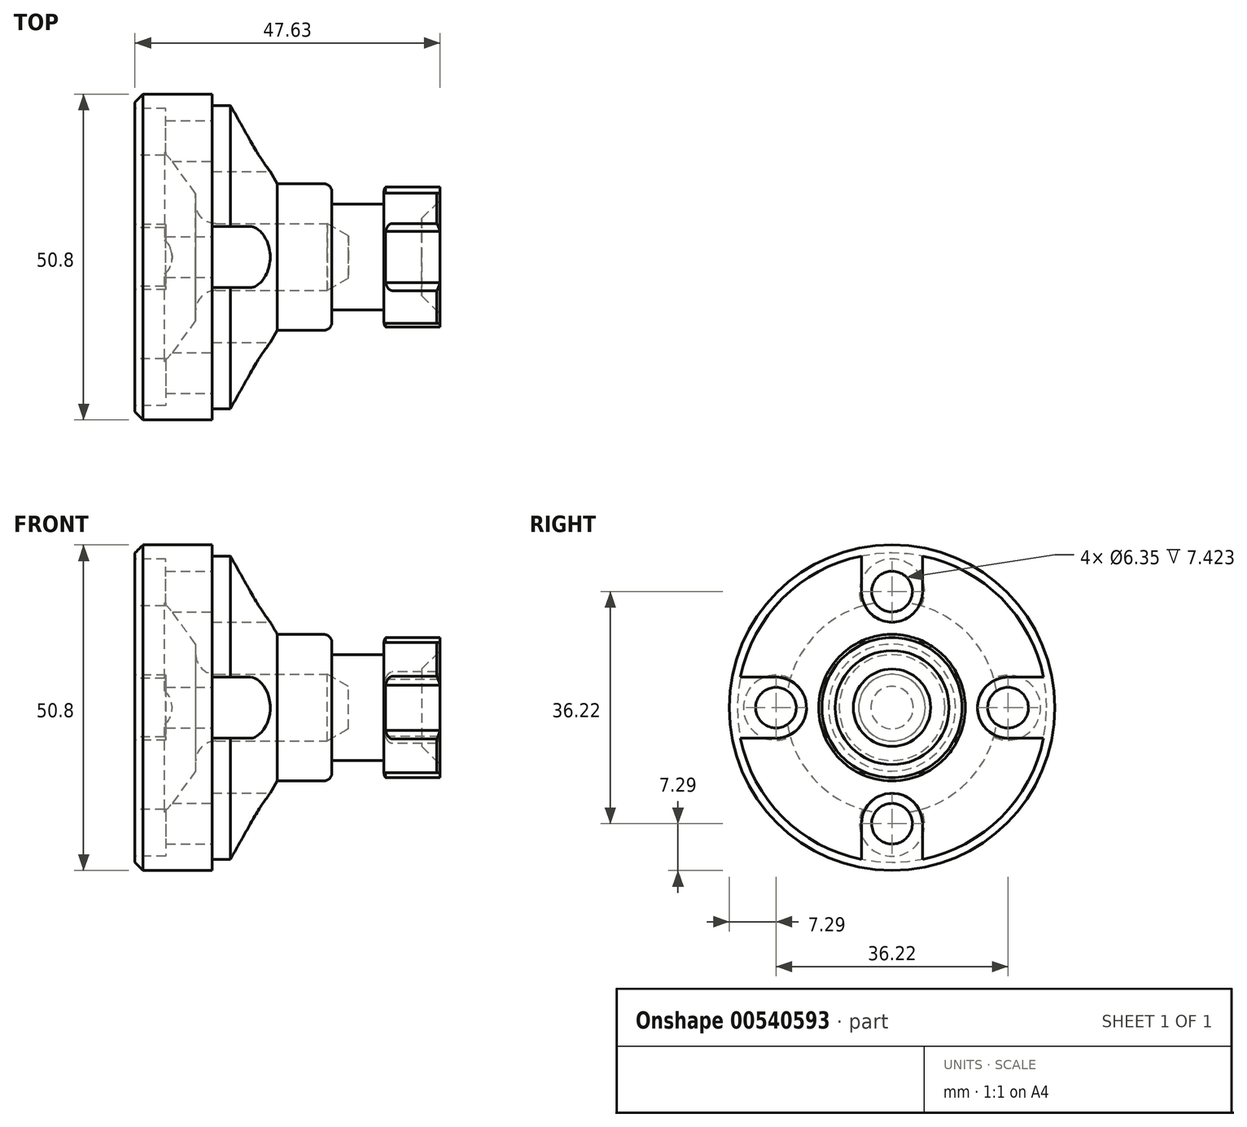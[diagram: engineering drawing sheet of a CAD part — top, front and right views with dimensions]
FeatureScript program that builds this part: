
annotation { "Feature Type Name" : "Feature", "Feature Type Description" : "" }
export const myFeature = defineFeature(function(context is Context, id is Id, definition is map)
    precondition{}
    {
        {
            var Q0;
            Q0=qCreatedBy(makeId("Front.planeOp"),FACE);
            var sketch = newSketch(context, id + "F0", { "sketchPlane" : qUnion([Q0])});
            skLineSegment(sketch, "E0", {"start": v(0, 0) * mm, "end": v(0, 10.92) * mm});
            skLineSegment(sketch, "E1", {"start": v(-35.56, 25.4) * mm, "end": v(-46.36, 25.4) * mm});
            skLineSegment(sketch, "E2", {"start": v(-47.63, 24.13) * mm, "end": v(-47.63, 0) * mm});
            skLineSegment(sketch, "E3", {"start": v(-47.63, 0) * mm, "end": v(0, 0) * mm});
            skLineSegment(sketch, "E4", {"start": v(-0.5, 11.43) * mm, "end": v(-7.5, 11.43) * mm});
            skLineSegment(sketch, "E5", {"start": v(-8.76, 10.16) * mm, "end": v(-8.76, 8.25) * mm});
            skLineSegment(sketch, "E6", {"start": v(-8.76, 8.25) * mm, "end": v(-16.9, 8.25) * mm});
            skLineSegment(sketch, "E7", {"start": v(-16.9, 10.16) * mm, "end": v(-16.9, 8.25) * mm});
            skLineSegment(sketch, "E8", {"start": v(-18.16, 11.43) * mm, "end": v(-25.4, 11.43) * mm});
            skLineSegment(sketch, "E9", {"start": v(-25.4, 11.43) * mm, "end": v(-32.73, 24.13) * mm});
            skLineSegment(sketch, "E10", {"start": v(-47.63, 0) * mm, "end": v(-47.63, 24.13) * mm, "construction": true});
            skLineSegment(sketch, "E11", {"start": v(-47.63, 24.13) * mm, "end": v(-46.36, 25.4) * mm});
            skPoint(sketch, "E12.orphan", {"position": v(-47.63, 25.4) * mm});
            skPoint(sketch, "E13.visualSharp", {"position": v(-16.9, 11.43) * mm});
            skArc(sketch, "E13.filletArc", {"start": v(-16.9, 10.16) * mm, "mid": v(-17.26, 11.06) * mm, "end": v(-18.16, 11.43) * mm});
            skPoint(sketch, "E14.visualSharp", {"position": v(-8.76, 11.43) * mm});
            skArc(sketch, "E14.filletArc", {"start": v(-7.5, 11.43) * mm, "mid": v(-8.4, 11.06) * mm, "end": v(-8.76, 10.16) * mm});
            skLineSegment(sketch, "E15", {"start": v(-0.5, 11.43) * mm, "end": v(0, 10.92) * mm});
            skPoint(sketch, "E16.orphan", {"position": v(0, 11.43) * mm});
            skLineSegment(sketch, "E17", {"start": v(-35.56, 24.13) * mm, "end": v(-35.56, 25.4) * mm});
            skLineSegment(sketch, "E18", {"start": v(-35.56, 24.13) * mm, "end": v(-32.73, 24.13) * mm});
            skSolve(sketch);
        }
        {
            var Q0;
            Q0=makeQuery(id+"F0.imprint","IMPRINT",FACE,{"disambiguationData":[TD([[makeQuery(id+"F0.imprint","IMPRINT",EDGE,{"derivedFrom":sQuery(id+"F0.wireOp",EDGE,"E1")}),1.0]])]});
            var Q1;
            Q1=sQuery(id+"F0.wireOp",EDGE,"E3");
            revolve(context, id + "F1", {"entities" : qUnion([Q0]), "axis" : qUnion([Q1]), "revolveType" : RevolveType.FULL});
        }
        {
            var Q0;
            Q0=makeQuery(id+"F1.opRevolve","SWEPT_FACE",FACE,{"disambiguationData":[OSD([sQuery(id+"F0.wireOp",EDGE,"E0")])]});
            var sketch = newSketch(context, id + "F2", { "sketchPlane" : qUnion([Q0])});
            skLineSegment(sketch, "E19", {"start": v(9.98, 0) * mm, "end": v(9.98, 10.16) * mm});
            skLineSegment(sketch, "E20", {"start": v(9.98, 10.16) * mm, "end": v(-0.18, 10.16) * mm});
            skLineSegment(sketch, "E21", {"start": v(-0.18, 10.16) * mm, "end": v(-10.34, 10.16) * mm});
            skLineSegment(sketch, "E22", {"start": v(-10.34, 10.16) * mm, "end": v(-10.34, -10.16) * mm});
            skLineSegment(sketch, "E23", {"start": v(-10.34, -10.16) * mm, "end": v(9.98, -10.16) * mm});
            skLineSegment(sketch, "E24", {"start": v(9.98, -10.16) * mm, "end": v(9.98, 0) * mm});
            skCircle(sketch, "E25", {"center": v(0, 0) * mm, "radius": 34.35 * mm});
            skSolve(sketch);
        }
        {
            var Q0;
            Q0=makeQuery(id+"F2.imprint","IMPRINT",FACE,{"disambiguationData":[TD([[makeQuery(id+"F2.imprint","IMPRINT",EDGE,{"derivedFrom":sQuery(id+"F2.wireOp",EDGE,"E25")}),1.0]])]});
            extrude(context, id + "F3", {"entities" : qUnion([Q0]), "operationType" : NewBodyOperationType.REMOVE, "oppositeDirection" : true, "depth" : 8.76 * mm, "offsetDistance" : 25.4 * mm});
        }
        {
            var Q0;
            Q0=qCreatedBy(makeId("Front.planeOp"),FACE);
            var sketch = newSketch(context, id + "F4", { "sketchPlane" : qUnion([Q0])});
            skLineSegment(sketch, "E26", {"start": v(0, 0) * mm, "end": v(-2.87, 0) * mm});
            skLineSegment(sketch, "E27", {"start": v(-2.87, 0) * mm, "end": v(-2.87, 6.03) * mm});
            skLineSegment(sketch, "E28", {"start": v(0, 0) * mm, "end": v(0, 8.9) * mm});
            skLineSegment(sketch, "E29", {"start": v(0, 8.9) * mm, "end": v(-2.87, 6.03) * mm});
            skSolve(sketch);
        }
        {
            var Q0;
            Q0 = qSketchRegion(id + "F4", true);
            var Q1;
            Q1=sQuery(id+"F4.wireOp",EDGE,"E26");
            revolve(context, id + "F5", {"operationType" : NewBodyOperationType.REMOVE, "entities" : qUnion([Q0]), "axis" : qUnion([Q1]), "revolveType" : RevolveType.FULL, "oppositeDirection" : true});
        }
        {
            var Q0;
            Q0=qCreatedBy(makeId("Right.planeOp"),FACE);
            var sketch = newSketch(context, id + "F6", { "sketchPlane" : qUnion([Q0])});
            skLineSegment(sketch, "E30", {"start": v(0, 13.35) * mm, "end": v(0, 14.94) * mm, "construction": true});
            skCircle(sketch, "E31", {"center": v(0, 18.11) * mm, "radius": 3.18 * mm});
            skArc(sketch, "E32", {"start": v(-4.76, 18.11) * mm, "mid": v(0, 13.35) * mm, "end": v(4.76, 18.11) * mm});
            skLineSegment(sketch, "E33", {"start": v(-4.76, 18.11) * mm, "end": v(-4.76, 25.69) * mm});
            skLineSegment(sketch, "E34", {"start": v(4.76, 18.11) * mm, "end": v(4.76, 25.69) * mm});
            skLineSegment(sketch, "E35", {"start": v(4.76, 25.69) * mm, "end": v(-4.76, 25.69) * mm});
            skCircle(sketch, "E36.1.0", {"center": v(-18.11, 0) * mm, "radius": 3.18 * mm});
            skArc(sketch, "E36.1.1", {"start": v(-18.11, -4.76) * mm, "mid": v(-13.35, 0) * mm, "end": v(-18.11, 4.76) * mm});
            skLineSegment(sketch, "E36.1.2", {"start": v(-25.69, 4.76) * mm, "end": v(-25.69, -4.76) * mm});
            skLineSegment(sketch, "E36.1.3", {"start": v(-18.11, -4.76) * mm, "end": v(-25.69, -4.76) * mm});
            skLineSegment(sketch, "E36.1.4", {"start": v(-18.11, 4.76) * mm, "end": v(-25.69, 4.76) * mm});
            skCircle(sketch, "E36.2.0", {"center": v(0, -18.11) * mm, "radius": 3.18 * mm});
            skArc(sketch, "E36.2.1", {"start": v(4.76, -18.11) * mm, "mid": v(0, -13.35) * mm, "end": v(-4.76, -18.11) * mm});
            skLineSegment(sketch, "E36.2.2", {"start": v(-4.76, -25.69) * mm, "end": v(4.76, -25.69) * mm});
            skLineSegment(sketch, "E36.2.3", {"start": v(4.76, -18.11) * mm, "end": v(4.76, -25.69) * mm});
            skLineSegment(sketch, "E36.2.4", {"start": v(-4.76, -18.11) * mm, "end": v(-4.76, -25.69) * mm});
            skCircle(sketch, "E36.3.0", {"center": v(18.11, 0) * mm, "radius": 3.18 * mm});
            skArc(sketch, "E36.3.1", {"start": v(18.11, 4.76) * mm, "mid": v(13.35, 0) * mm, "end": v(18.11, -4.76) * mm});
            skLineSegment(sketch, "E36.3.2", {"start": v(25.69, -4.76) * mm, "end": v(25.69, 4.76) * mm});
            skLineSegment(sketch, "E36.3.3", {"start": v(18.11, 4.76) * mm, "end": v(25.69, 4.76) * mm});
            skLineSegment(sketch, "E36.3.4", {"start": v(18.11, -4.76) * mm, "end": v(25.69, -4.76) * mm});
            skPoint(sketch, "E36.center", {"position": v(0, 0) * mm});
            skSolve(sketch);
        }
        {
            var Q0;
            Q0 = qSketchRegion(id + "F6", true);
            extrude(context, id + "F7", {"entities" : qUnion([Q0]), "operationType" : NewBodyOperationType.REMOVE, "oppositeDirection" : true, "depth" : 35.56 * mm, "offsetDistance" : 25.4 * mm});
        }
        {
            var Q0;
            Q0=qCreatedBy(makeId("Right.planeOp"),FACE);
            var sketch = newSketch(context, id + "F8", { "sketchPlane" : qUnion([Q0])});
            skCircle(sketch, "E37", {"center": v(0, 18.11) * mm, "radius": 3.18 * mm});
            skCircle(sketch, "E38.1.0", {"center": v(-18.11, 0) * mm, "radius": 3.18 * mm});
            skCircle(sketch, "E38.2.0", {"center": v(0, -18.11) * mm, "radius": 3.18 * mm});
            skCircle(sketch, "E38.3.0", {"center": v(18.11, 0) * mm, "radius": 3.18 * mm});
            skPoint(sketch, "E38.center", {"position": v(0, 0) * mm});
            skSolve(sketch);
        }
        {
            var Q0;
            Q0=makeQuery(id+"F8.imprint","IMPRINT",FACE,{"disambiguationData":[TD([[makeQuery(id+"F8.imprint","IMPRINT",EDGE,{"derivedFrom":sQuery(id+"F8.wireOp",EDGE,"E37")}),1.0]])]});
            var Q1;
            Q1=makeQuery(id+"F8.imprint","IMPRINT",FACE,{"disambiguationData":[TD([[makeQuery(id+"F8.imprint","IMPRINT",EDGE,{"derivedFrom":sQuery(id+"F8.wireOp",EDGE,"E38.3.0")}),1.0]])]});
            var Q2;
            Q2=makeQuery(id+"F8.imprint","IMPRINT",FACE,{"disambiguationData":[TD([[makeQuery(id+"F8.imprint","IMPRINT",EDGE,{"derivedFrom":sQuery(id+"F8.wireOp",EDGE,"E38.2.0")}),1.0]])]});
            var Q3;
            Q3=makeQuery(id+"F8.imprint","IMPRINT",FACE,{"disambiguationData":[TD([[makeQuery(id+"F8.imprint","IMPRINT",EDGE,{"derivedFrom":sQuery(id+"F8.wireOp",EDGE,"E38.1.0")}),1.0]])]});
            extrude(context, id + "F9", {"entities" : qUnion([Q0, Q1, Q2, Q3]), "operationType" : NewBodyOperationType.REMOVE, "endBound" : BoundingType.THROUGH_ALL, "oppositeDirection" : true, "depth" : 25.4 * mm, "offsetDistance" : 25.4 * mm});
        }
        {
            var Q0;
            Q0=qCreatedBy(makeId("Front.planeOp"),FACE);
            var sketch = newSketch(context, id + "F10", { "sketchPlane" : qUnion([Q0])});
            skLineSegment(sketch, "E39", {"start": v(-47.62, 0) * mm, "end": v(-14.32, 0) * mm});
            skLineSegment(sketch, "E40", {"start": v(-14.32, 0) * mm, "end": v(-14.32, 3.3) * mm});
            skLineSegment(sketch, "E41", {"start": v(-47.62, 0) * mm, "end": v(-47.62, 5.2) * mm});
            skLineSegment(sketch, "E42", {"start": v(-47.62, 5.2) * mm, "end": v(-17.62, 5.2) * mm});
            skLineSegment(sketch, "E43", {"start": v(-14.32, 3.3) * mm, "end": v(-17.62, 5.2) * mm});
            skSolve(sketch);
        }
        {
            var Q0;
            Q0 = qSketchRegion(id + "F10", true);
            var Q1;
            Q1=sQuery(id+"F10.wireOp",EDGE,"E39");
            revolve(context, id + "F11", {"operationType" : NewBodyOperationType.REMOVE, "entities" : qUnion([Q0]), "axis" : qUnion([Q1]), "revolveType" : RevolveType.FULL, "oppositeDirection" : true});
        }
        {
            var Q0;
            Q0=qCreatedBy(makeId("Front.planeOp"),FACE);
            var sketch = newSketch(context, id + "F12", { "sketchPlane" : qUnion([Q0])});
            skLineSegment(sketch, "E44", {"start": v(-38.16, 0) * mm, "end": v(-47.8, 0) * mm});
            skLineSegment(sketch, "E45", {"start": v(-47.8, 0) * mm, "end": v(-47.8, 16.51) * mm});
            skLineSegment(sketch, "E46", {"start": v(-47.8, 16.51) * mm, "end": v(-42.98, 16.51) * mm});
            skLineSegment(sketch, "E47", {"start": v(-47.8, 0) * mm, "end": v(-38.16, 0) * mm, "construction": true});
            skLineSegment(sketch, "E48", {"start": v(-38.16, 0) * mm, "end": v(-38.16, 9.9) * mm});
            skLineSegment(sketch, "E49", {"start": v(-38.16, 9.9) * mm, "end": v(-42.98, 16.5) * mm});
            skSolve(sketch);
        }
        {
            var Q0;
            Q0 = qSketchRegion(id + "F12", true);
            var Q1;
            Q1=sQuery(id+"F12.wireOp",EDGE,"E44");
            revolve(context, id + "F13", {"operationType" : NewBodyOperationType.REMOVE, "entities" : qUnion([Q0]), "axis" : qUnion([Q1]), "revolveType" : RevolveType.FULL, "oppositeDirection" : true});
        }
        {
            var Q0;
            Q0=makeQuery(id+"F13.boolean.opBoolean","INTERSECT",EDGE,{"derivedFrom":[makeQuery(id+"F11.boolean.opBoolean","COPY",FACE,{"derivedFrom":makeQuery(id+"F11.opRevolve","SWEPT_FACE",FACE,{"disambiguationData":[OSD([sQuery(id+"F10.wireOp",EDGE,"E42")])]})}),makeQuery(id+"F13.opRevolve","SWEPT_FACE",FACE,{"disambiguationData":[OSD([sQuery(id+"F12.wireOp",EDGE,"E48")])]})]});
            fillet(context, id + "F14", {"entities" : qUnion([Q0]), "radius" : 3.17 * mm, "tangentPropagation" : true, "allowEdgeOverflow" : false});
        }
        {
            var Q0;
            Q0=makeQuery(id+"F1.opRevolve","SWEPT_FACE",FACE,{"disambiguationData":[OSD([sQuery(id+"F0.wireOp",EDGE,"E2")])]});
            var sketch = newSketch(context, id + "F15", { "sketchPlane" : qUnion([Q0])});
            skLineSegment(sketch, "E50", {"start": v(0, 0) * mm, "end": v(0, 18.11) * mm, "construction": true});
            skCircle(sketch, "E51", {"center": v(0, 18.11) * mm, "radius": 5.08 * mm});
            skCircle(sketch, "E52.1.0", {"center": v(-18.11, 0) * mm, "radius": 5.08 * mm});
            skCircle(sketch, "E52.2.0", {"center": v(0, -18.11) * mm, "radius": 5.08 * mm});
            skCircle(sketch, "E52.3.0", {"center": v(18.11, 0) * mm, "radius": 5.08 * mm});
            skPoint(sketch, "E52.center", {"position": v(0, 0) * mm});
            skSolve(sketch);
        }
        {
            var Q0;
            {var subQ2=makeQuery(id+"F1.opRevolve","SWEPT_FACE",FACE,{"disambiguationData":[OSD([sQuery(id+"F0.wireOp",EDGE,"E2")])]});var subQ8=makeQuery(id+"F9.boolean.opBoolean","INTERSECT",EDGE,{"derivedFrom":[subQ2,makeQuery(id+"F9.opExtrude","SWEPT_FACE",FACE,{"disambiguationData":[OSD([sQuery(id+"F8.wireOp",EDGE,"E37")])]})]});Q0=makeQuery(id+"F15.imprint","IMPRINT",FACE,{"disambiguationData":[TD([[makeQuery(id+"F15.imprint","IMPRINT",EDGE,{"derivedFrom":subQ8}),1.0]])]});}
            var Q1;
            {var subQ2=makeQuery(id+"F1.opRevolve","SWEPT_FACE",FACE,{"disambiguationData":[OSD([sQuery(id+"F0.wireOp",EDGE,"E2")])]});var subQ8=makeQuery(id+"F9.boolean.opBoolean","INTERSECT",EDGE,{"derivedFrom":[subQ2,makeQuery(id+"F9.opExtrude","SWEPT_FACE",FACE,{"disambiguationData":[OSD([sQuery(id+"F8.wireOp",EDGE,"E38.3.0")])]})]});Q1=makeQuery(id+"F15.imprint","IMPRINT",FACE,{"disambiguationData":[TD([[makeQuery(id+"F15.imprint","IMPRINT",EDGE,{"derivedFrom":subQ8}),1.0]])]});}
            var Q2;
            {var subQ2=makeQuery(id+"F1.opRevolve","SWEPT_FACE",FACE,{"disambiguationData":[OSD([sQuery(id+"F0.wireOp",EDGE,"E2")])]});var subQ8=makeQuery(id+"F9.boolean.opBoolean","INTERSECT",EDGE,{"derivedFrom":[subQ2,makeQuery(id+"F9.opExtrude","SWEPT_FACE",FACE,{"disambiguationData":[OSD([sQuery(id+"F8.wireOp",EDGE,"E38.1.0")])]})]});Q2=makeQuery(id+"F15.imprint","IMPRINT",FACE,{"disambiguationData":[TD([[makeQuery(id+"F15.imprint","IMPRINT",EDGE,{"derivedFrom":subQ8}),1.0]])]});}
            var Q3;
            {var subQ2=makeQuery(id+"F1.opRevolve","SWEPT_FACE",FACE,{"disambiguationData":[OSD([sQuery(id+"F0.wireOp",EDGE,"E2")])]});var subQ8=makeQuery(id+"F9.boolean.opBoolean","INTERSECT",EDGE,{"derivedFrom":[subQ2,makeQuery(id+"F9.opExtrude","SWEPT_FACE",FACE,{"disambiguationData":[OSD([sQuery(id+"F8.wireOp",EDGE,"E38.2.0")])]})]});Q3=makeQuery(id+"F15.imprint","IMPRINT",FACE,{"disambiguationData":[TD([[makeQuery(id+"F15.imprint","IMPRINT",EDGE,{"derivedFrom":subQ8}),1.0]])]});}
            extrude(context, id + "F16", {"entities" : qUnion([Q0, Q1, Q2, Q3]), "operationType" : NewBodyOperationType.REMOVE, "oppositeDirection" : true, "depth" : 4.83 * mm, "offsetDistance" : 25.4 * mm});
        }
    });
